# Revit family: EKF_EE_ДверьFORT_IP54_PROxima
name_source: partatom
category: Электрооборудование
units: mm (PartAtom-declared; Revit-internal decimal feet)

## family parameters
Всегда вертикально = Нет
На основе рабочей плоскости = Да
Общий = Да
При загрузке вырезать с полостями = Нет
Размер круглого соединителя = Использовать диаметр
Тип детали = Силовой щит
Точка расчета площади = Нет

## types (8) — shared parameters
ADSK_Единица измерения = шт.
ADSK_Завод-изготовитель = EKF
ADSK_Количество = 1
ADSK_Марка = Дверь FORT
ADSK_Материал = RAL 7035_Сталь
ADSK_Обозначение = Дверь FORT
ADSK_Размер_Глубина = 21 мм
Изготовитель = EKF
КолОтв = 4
Серия номенклатуры = PROxima
Степень защиты IP = IP54
ТВ = EKF_2
Тип установки = -
zero-valued in all types: ADSK_Масса, Отметка по умолчанию

## per-type parameters (varying)
| type | ADSK_Код изделия | ADSK_Размер_Высота | ADSK_Размер_Ширина | Карман для документации | Тип |
| Дверь FORT для корпуса высотой 1800 и шириной 600 IP54 EKF PROxima | FD186G | 1800 мм | 591.5 мм | Да | 373 мм |
| Дверь FORT для корпуса высотой 1800 и шириной 800 IP54 EKF PROxima | FD188G | 1800 мм | 791.5 мм | Да | 375 мм |
| Дверь FORT для корпуса высотой 2000 и шириной 400 IP54 EKF PROxima | FD204G | 2000 мм | 391.5 мм | Нет | 377 мм |
| Дверь FORT для корпуса высотой 2000 и шириной 600 IP54 EKF PROxima | FD206G | 2000 мм | 591.5 мм | Да | 379 мм |
| Дверь FORT для корпуса высотой 2000 и шириной 800 IP54 EKF PROxima | FD208G | 2000 мм | 791.5 мм | Да | 381 мм |
| Дверь FORT для корпуса высотой 2200 и шириной 400 IP54 EKF PROxima | FD224G | 2200 мм | 391.5 мм | Нет | 383 мм |
| Дверь FORT для корпуса высотой 2200 и шириной 600 IP54 EKF PROxima | FD226G | 2200 мм | 591.5 мм | Да | 385 мм |
| Дверь FORT для корпуса высотой 2200 и шириной 800 IP54 EKF PROxima | FD228G | 2200 мм | 791.5 мм | Да | 387 мм |

note: column(s) folded — value = type name in every type: ADSK_Наименование
